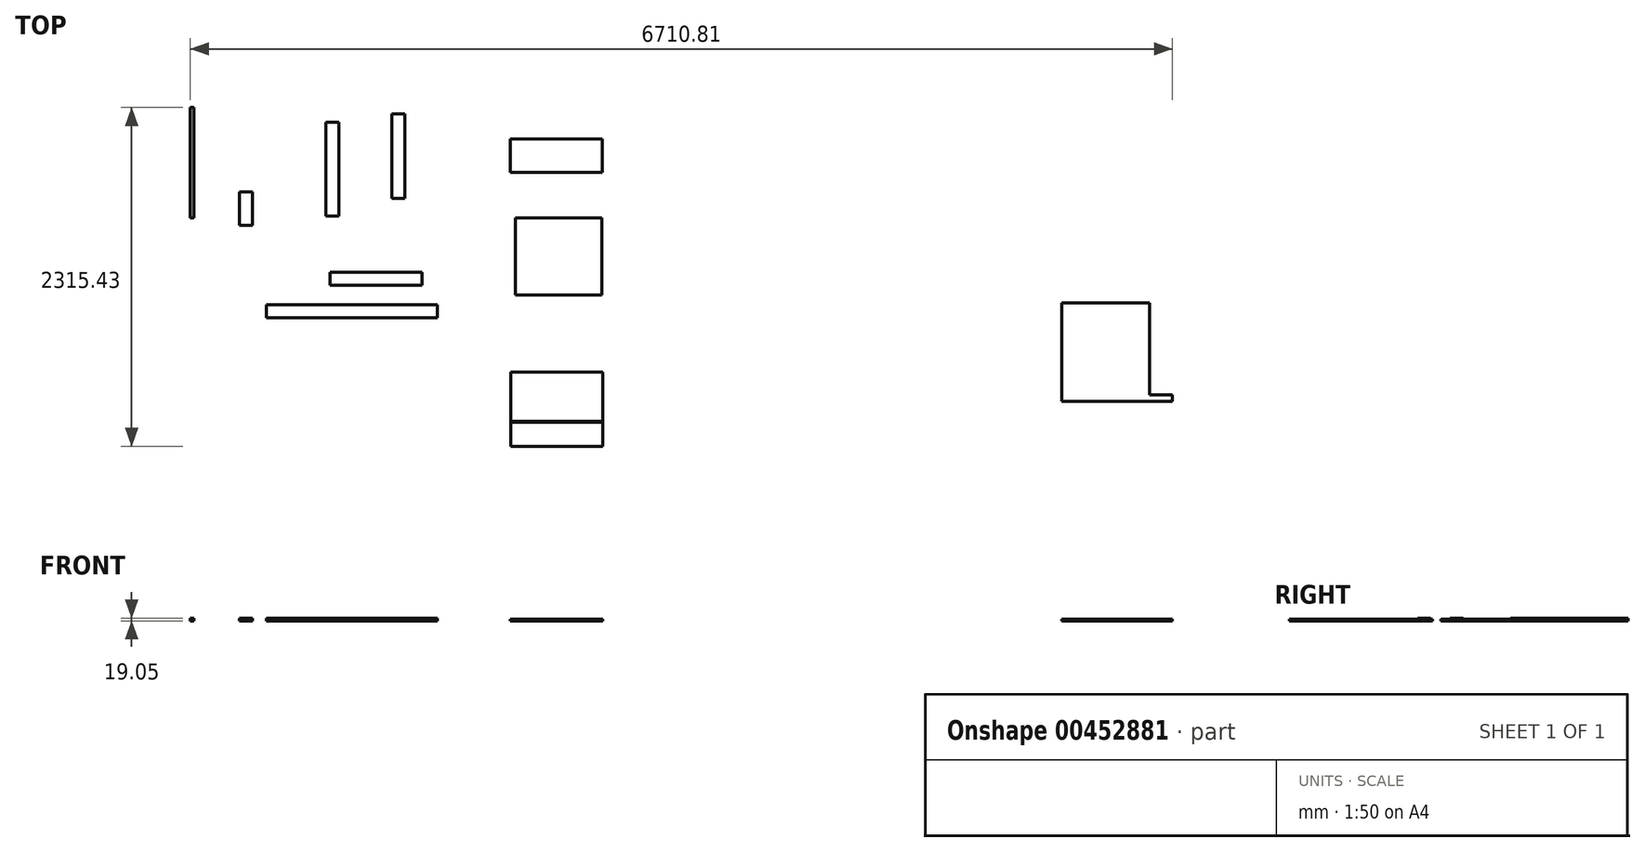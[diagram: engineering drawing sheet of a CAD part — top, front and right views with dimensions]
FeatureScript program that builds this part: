
annotation { "Feature Type Name" : "Feature", "Feature Type Description" : "" }
export const myFeature = defineFeature(function(context is Context, id is Id, definition is map)
    precondition{}
    {
        {
            var Q0;
            Q0=qCreatedBy(makeId("Top.planeOp"),FACE);
            var sketch = newSketch(context, id + "F0", { "sketchPlane" : qUnion([Q0])});
            skLineSegment(sketch, "E0.bottom", {"start": v(-62.28, 39.1) * mm, "end": v(26.62, 39.1) * mm});
            skLineSegment(sketch, "E0.top", {"start": v(-62.28, 616.95) * mm, "end": v(26.62, 616.95) * mm});
            skLineSegment(sketch, "E0.left", {"start": v(-62.28, 39.1) * mm, "end": v(-62.28, 616.95) * mm});
            skLineSegment(sketch, "E0.right", {"start": v(26.62, 39.1) * mm, "end": v(26.62, 616.95) * mm});
            skLineSegment(sketch, "E1.bottom", {"start": v(-481.64, -465.3) * mm, "end": v(147, -465.3) * mm});
            skLineSegment(sketch, "E1.top", {"start": v(-481.64, -554.2) * mm, "end": v(147, -554.2) * mm});
            skLineSegment(sketch, "E1.left", {"start": v(-481.64, -465.3) * mm, "end": v(-481.64, -554.2) * mm});
            skLineSegment(sketch, "E1.right", {"start": v(147, -465.3) * mm, "end": v(147, -554.2) * mm});
            skLineSegment(sketch, "E2.bottom", {"start": v(-917.9, -688.46) * mm, "end": v(250.5, -688.46) * mm});
            skLineSegment(sketch, "E2.top", {"start": v(-917.9, -777.36) * mm, "end": v(250.5, -777.36) * mm});
            skLineSegment(sketch, "E2.left", {"start": v(-917.9, -688.46) * mm, "end": v(-917.9, -777.36) * mm});
            skLineSegment(sketch, "E2.right", {"start": v(250.5, -688.46) * mm, "end": v(250.5, -777.36) * mm});
            skSolve(sketch);
        }
        {
            var Q0;
            Q0 = qSketchRegion(id + "F0", true);
            extrude(context, id + "F1", {"entities" : qUnion([Q0]), "depth" : 19.05 * mm});
        }
        {
            var Q0;
            Q0=qCreatedBy(makeId("Top.planeOp"),FACE);
            var sketch = newSketch(context, id + "F2", { "sketchPlane" : qUnion([Q0])});
            skLineSegment(sketch, "E3.bottom", {"start": v(-512.02, 559.06) * mm, "end": v(-423.12, 559.06) * mm});
            skLineSegment(sketch, "E3.top", {"start": v(-512.02, -82.29) * mm, "end": v(-423.12, -82.29) * mm});
            skLineSegment(sketch, "E3.left", {"start": v(-512.02, 559.06) * mm, "end": v(-512.02, -82.29) * mm});
            skLineSegment(sketch, "E3.right", {"start": v(-423.12, 559.06) * mm, "end": v(-423.12, -82.29) * mm});
            skLineSegment(sketch, "E4.bottom", {"start": v(-1012.06, 84.6) * mm, "end": v(-1100.96, 84.6) * mm});
            skLineSegment(sketch, "E4.top", {"start": v(-1012.06, -144) * mm, "end": v(-1100.96, -144) * mm});
            skLineSegment(sketch, "E4.left", {"start": v(-1012.06, 84.6) * mm, "end": v(-1012.06, -144) * mm});
            skLineSegment(sketch, "E4.right", {"start": v(-1100.96, 84.6) * mm, "end": v(-1100.96, -144) * mm});
            skLineSegment(sketch, "E5.bottom", {"start": v(-1437.96, 661.11) * mm, "end": v(-1412.56, 661.11) * mm});
            skLineSegment(sketch, "E5.top", {"start": v(-1437.96, -94.54) * mm, "end": v(-1412.56, -94.54) * mm});
            skLineSegment(sketch, "E5.left", {"start": v(-1437.96, 661.11) * mm, "end": v(-1437.96, -94.54) * mm});
            skLineSegment(sketch, "E5.right", {"start": v(-1412.56, 661.11) * mm, "end": v(-1412.56, -94.54) * mm});
            skSolve(sketch);
        }
        {
            var Q0;
            Q0 = qSketchRegion(id + "F2", true);
            extrude(context, id + "F3", {"entities" : qUnion([Q0]), "depth" : 19.05 * mm});
        }
        {
            var Q0;
            Q0=qCreatedBy(makeId("Top.planeOp"),FACE);
            var sketch = newSketch(context, id + "F4", { "sketchPlane" : qUnion([Q0])});
            skLineSegment(sketch, "E6.bottom", {"start": v(748.57, 446.24) * mm, "end": v(1377.22, 446.24) * mm});
            skLineSegment(sketch, "E6.top", {"start": v(748.57, 217.64) * mm, "end": v(1377.22, 217.64) * mm});
            skLineSegment(sketch, "E6.left", {"start": v(748.57, 446.24) * mm, "end": v(748.57, 217.64) * mm});
            skLineSegment(sketch, "E6.right", {"start": v(1377.22, 446.24) * mm, "end": v(1377.22, 217.64) * mm});
            skLineSegment(sketch, "E7.bottom", {"start": v(783.5, -92.47) * mm, "end": v(1374.04, -92.47) * mm});
            skLineSegment(sketch, "E7.top", {"start": v(783.5, -619.52) * mm, "end": v(1374.04, -619.52) * mm});
            skLineSegment(sketch, "E7.left", {"start": v(783.5, -92.47) * mm, "end": v(783.5, -619.52) * mm});
            skLineSegment(sketch, "E7.right", {"start": v(1374.04, -92.47) * mm, "end": v(1374.04, -619.52) * mm});
            skLineSegment(sketch, "E8.bottom", {"start": v(752.92, -1146.32) * mm, "end": v(1381.57, -1146.32) * mm});
            skLineSegment(sketch, "E8.top", {"start": v(752.92, -1654.32) * mm, "end": v(1381.57, -1654.32) * mm});
            skLineSegment(sketch, "E8.left", {"start": v(752.92, -1146.32) * mm, "end": v(752.92, -1654.32) * mm});
            skLineSegment(sketch, "E8.right", {"start": v(1381.57, -1146.32) * mm, "end": v(1381.57, -1654.32) * mm});
            skSolve(sketch);
        }
        {
            var Q0;
            Q0 = qSketchRegion(id + "F4", true);
            extrude(context, id + "F5", {"entities" : qUnion([Q0]), "depth" : 12.7 * mm});
        }
        {
            var Q0;
            Q0=qCreatedBy(makeId("Top.planeOp"),FACE);
            var sketch = newSketch(context, id + "F6", { "sketchPlane" : qUnion([Q0])});
            skLineSegment(sketch, "E9.bottom", {"start": v(4517.2, -674.51) * mm, "end": v(5117.4, -674.51) * mm});
            skLineSegment(sketch, "E9.top", {"start": v(4517.2, -1347.61) * mm, "end": v(5117.4, -1347.61) * mm});
            skLineSegment(sketch, "E9.left", {"start": v(4517.2, -674.51) * mm, "end": v(4517.2, -1347.61) * mm});
            skLineSegment(sketch, "E9.right", {"start": v(5117.4, -674.51) * mm, "end": v(5117.4, -1303.16) * mm});
            skLineSegment(sketch, "E10", {"start": v(4517.2, -1347.61) * mm, "end": v(5272.85, -1347.61) * mm});
            skLineSegment(sketch, "E11", {"start": v(5117.4, -1303.16) * mm, "end": v(5272.85, -1303.16) * mm});
            skLineSegment(sketch, "E12", {"start": v(5272.85, -1303.16) * mm, "end": v(5272.85, -1347.61) * mm});
            skSolve(sketch);
        }
        {
            var Q0;
            Q0 = qSketchRegion(id + "F6", true);
            extrude(context, id + "F7", {"entities" : qUnion([Q0]), "depth" : 12.7 * mm});
        }
        {
            var Q0;
            Q0=makeQuery(id+"F5.opExtrude","CAP_FACE",FACE,{"disambiguationData":[OSD([sQuery(id+"F4.wireOp",EDGE,"E8.bottom"),sQuery(id+"F4.wireOp",EDGE,"E8.top"),sQuery(id+"F4.wireOp",EDGE,"E8.left"),sQuery(id+"F4.wireOp",EDGE,"E8.right")])],"isStart":false});
            var sketch = newSketch(context, id + "F8", { "sketchPlane" : qUnion([Q0])});
            skLineSegment(sketch, "E13", {"start": v(1067.25, -1146.32) * mm, "end": v(1067.25, -1489.22) * mm});
            skLineSegment(sketch, "E14", {"start": v(1067.25, -1489.22) * mm, "end": v(1381.57, -1489.22) * mm});
            skLineSegment(sketch, "E15", {"start": v(1381.57, -1489.22) * mm, "end": v(752.92, -1489.22) * mm});
            skLineSegment(sketch, "E16.0", {"start": v(1381.57, -1482.87) * mm, "end": v(752.92, -1482.87) * mm});
            skSolve(sketch);
        }
        {
            var Q0;
            {var subQ0=sQuery(id+"F8.wireOp",EDGE,"E15");var subQ1=sQuery(id+"F8.wireOp",EDGE,"E13");var subQ2=makeQuery(id+"F8.imprint","INTERSECT",VERTEX,{"derivedFrom":[subQ1,subQ0]});Q0=makeQuery(id+"F8.imprint","IMPRINT",FACE,{"disambiguationData":[TD([[makeQuery(id+"F8.imprint","IMPRINT",EDGE,{"disambiguationData":[TD([[subQ2,1.0]])],"derivedFrom":subQ1}),-1.0]])]});}
            var Q1;
            {var subQ0=sQuery(id+"F8.wireOp",EDGE,"E15");var subQ1=sQuery(id+"F8.wireOp",EDGE,"E13");var subQ2=makeQuery(id+"F8.imprint","INTERSECT",VERTEX,{"derivedFrom":[subQ1,subQ0]});Q1=makeQuery(id+"F8.imprint","IMPRINT",FACE,{"disambiguationData":[TD([[makeQuery(id+"F8.imprint","IMPRINT",EDGE,{"disambiguationData":[TD([[subQ2,1.0]])],"derivedFrom":subQ1}),1.0]])]});}
            extrude(context, id + "F9", {"entities" : qUnion([Q0, Q1]), "operationType" : NewBodyOperationType.REMOVE, "oppositeDirection" : true, "depth" : 2.54 * mm});
        }
    });
